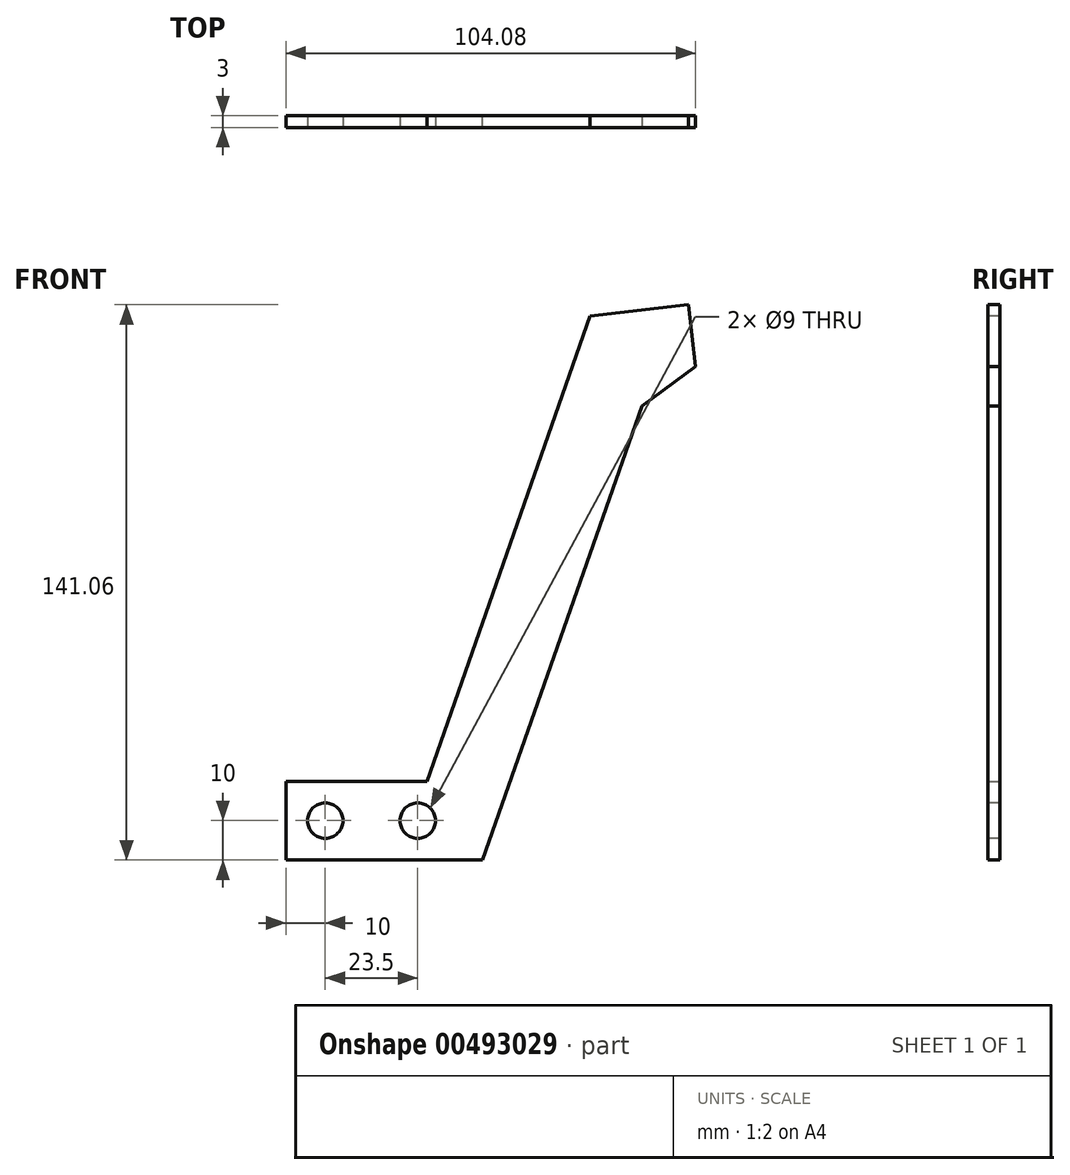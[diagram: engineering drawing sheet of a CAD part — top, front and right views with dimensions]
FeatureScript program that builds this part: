
annotation { "Feature Type Name" : "Feature", "Feature Type Description" : "" }
export const myFeature = defineFeature(function(context is Context, id is Id, definition is map)
    precondition{}
    {
        {
            var Q0;
            Q0=qCreatedBy(makeId("Front.planeOp"),FACE);
            var sketch = newSketch(context, id + "F0", { "sketchPlane" : qUnion([Q0])});
            skLineSegment(sketch, "E0.bottom", {"start": v(0, 0) * mm, "end": v(50, 0) * mm});
            skLineSegment(sketch, "E0.top", {"start": v(0, 20) * mm, "end": v(50, 20) * mm});
            skLineSegment(sketch, "E0.left", {"start": v(0, 0) * mm, "end": v(0, 20) * mm});
            skLineSegment(sketch, "E0.right", {"start": v(50, 0) * mm, "end": v(50, 20) * mm});
            skSolve(sketch);
        }
        {
            var Q0;
            Q0 = qSketchRegion(id + "F0", true);
            extrude(context, id + "F1", {"entities" : qUnion([Q0]), "depth" : 3 * mm});
        }
        {
            var Q0;
            Q0=makeQuery(id+"F1.opExtrude","CAP_FACE",FACE,{"disambiguationData":[OSD([sQuery(id+"F0.wireOp",EDGE,"E0.bottom"),sQuery(id+"F0.wireOp",EDGE,"E0.top"),sQuery(id+"F0.wireOp",EDGE,"E0.left"),sQuery(id+"F0.wireOp",EDGE,"E0.right")])],"isStart":false});
            var sketch = newSketch(context, id + "F2", { "sketchPlane" : qUnion([Q0])});
            skCircle(sketch, "E1", {"center": v(10, 10) * mm, "radius": 4.5 * mm});
            skCircle(sketch, "E2", {"center": v(33.5, 10) * mm, "radius": 4.5 * mm});
            skLineSegment(sketch, "E3", {"start": v(10, 10) * mm, "end": v(33.5, 10) * mm, "construction": true});
            skSolve(sketch);
        }
        {
            var Q0;
            Q0 = qSketchRegion(id + "F2", true);
            extrude(context, id + "F3", {"entities" : qUnion([Q0]), "operationType" : NewBodyOperationType.REMOVE, "endBound" : BoundingType.THROUGH_ALL, "oppositeDirection" : true, "depth" : 25 * mm});
        }
        {
            var Q0;
            Q0=makeQuery(id+"F1.opExtrude","CAP_FACE",FACE,{"disambiguationData":[OSD([sQuery(id+"F0.wireOp",EDGE,"E0.bottom"),sQuery(id+"F0.wireOp",EDGE,"E0.top"),sQuery(id+"F0.wireOp",EDGE,"E0.left"),sQuery(id+"F0.wireOp",EDGE,"E0.right")])],"isStart":false});
            var sketch = newSketch(context, id + "F4", { "sketchPlane" : qUnion([Q0])});
            skLineSegment(sketch, "E4", {"start": v(50, 0) * mm, "end": v(90.48, 115.34) * mm});
            skLineSegment(sketch, "E5", {"start": v(90.48, 115.34) * mm, "end": v(104.08, 125.39) * mm});
            skLineSegment(sketch, "E6", {"start": v(104.08, 125.39) * mm, "end": v(102.31, 141.06) * mm});
            skLineSegment(sketch, "E7", {"start": v(102.31, 141.06) * mm, "end": v(77.32, 138.24) * mm});
            skLineSegment(sketch, "E8", {"start": v(77.32, 138.24) * mm, "end": v(35.82, 20) * mm});
            skLineSegment(sketch, "E9", {"start": v(35.82, 20) * mm, "end": v(50, 20) * mm});
            skLineSegment(sketch, "E10", {"start": v(50, 20) * mm, "end": v(50, 0) * mm});
            skCircle(sketch, "E11", {"center": v(93.5, 130) * mm, "radius": 4.5 * mm, "construction": true});
            skLineSegment(sketch, "E12", {"start": v(33.5, 10) * mm, "end": v(93.5, 10) * mm, "construction": true});
            skPoint(sketch, "E12.endSnap0", {"position": v(50, 10) * mm});
            skLineSegment(sketch, "E13", {"start": v(93.5, 10) * mm, "end": v(93.5, 130) * mm, "construction": true});
            skSolve(sketch);
        }
        {
            var Q0;
            Q0 = qSketchRegion(id + "F4", true);
            var Q1;
            Q1=makeQuery(id+"F1.opExtrude","CAP_FACE",FACE,{"disambiguationData":[OSD([sQuery(id+"F0.wireOp",EDGE,"E0.bottom"),sQuery(id+"F0.wireOp",EDGE,"E0.top"),sQuery(id+"F0.wireOp",EDGE,"E0.left"),sQuery(id+"F0.wireOp",EDGE,"E0.right")])],"isStart":true});
            extrude(context, id + "F5", {"entities" : qUnion([Q0]), "operationType" : NewBodyOperationType.ADD, "endBound" : BoundingType.UP_TO_SURFACE, "oppositeDirection" : true, "endBoundEntityFace" : qUnion([Q1]), "depth" : 25 * mm});
        }
    });
